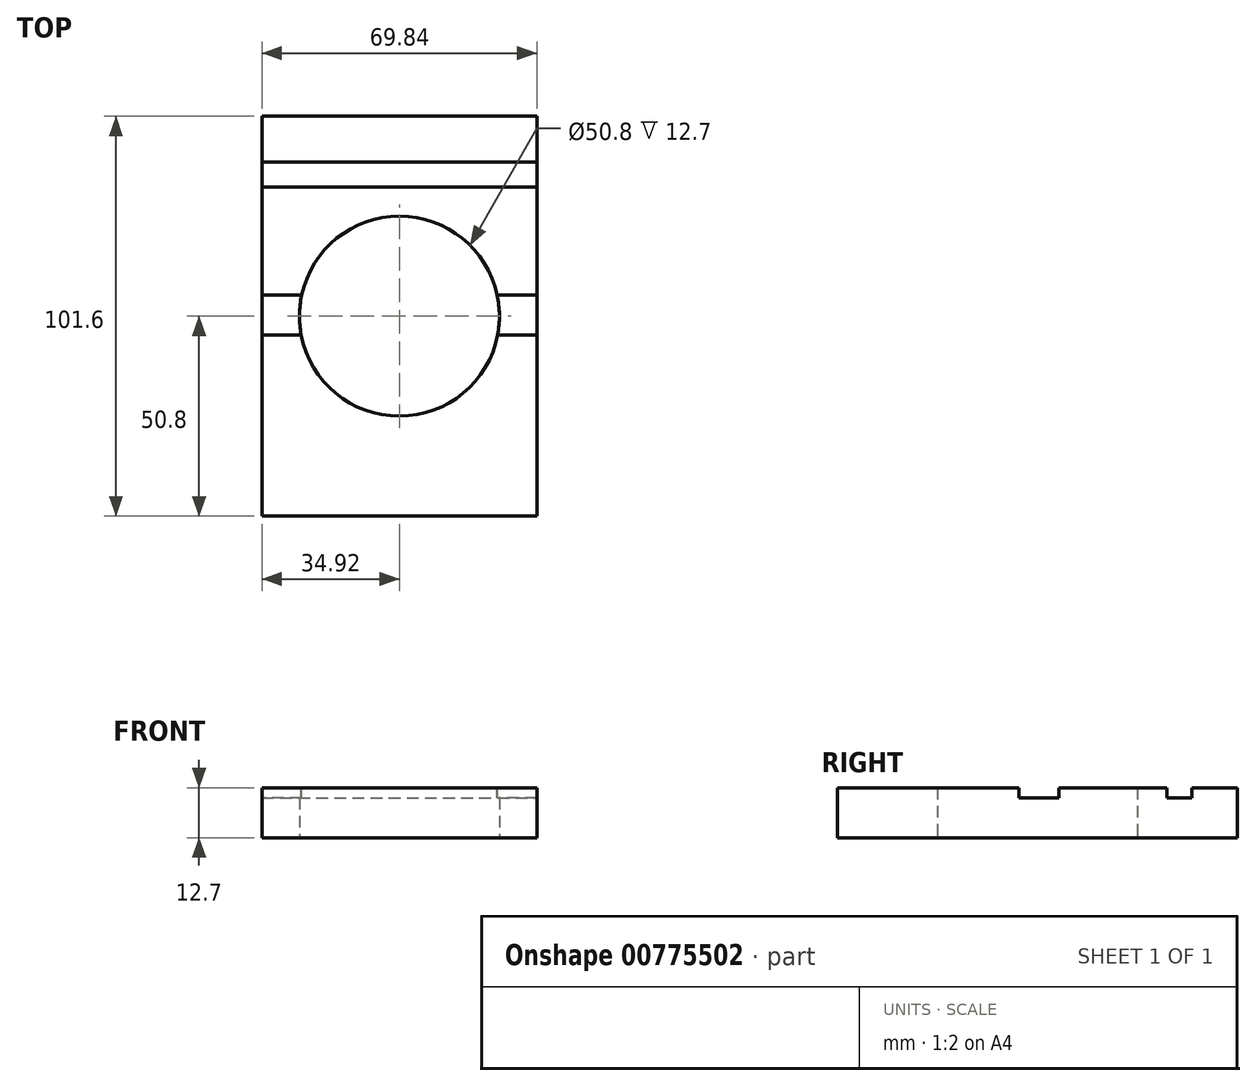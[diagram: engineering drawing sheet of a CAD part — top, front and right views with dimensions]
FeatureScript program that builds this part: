
annotation { "Feature Type Name" : "Feature", "Feature Type Description" : "" }
export const myFeature = defineFeature(function(context is Context, id is Id, definition is map)
    precondition{}
    {
        {
            var Q0;
            Q0=qCreatedBy(makeId("Top.planeOp"),FACE);
            var sketch = newSketch(context, id + "F0", { "sketchPlane" : qUnion([Q0])});
            skLineSegment(sketch, "E0.bottom", {"start": v(34.93, 50.8) * mm, "end": v(-34.92, 50.8) * mm});
            skLineSegment(sketch, "E0.top", {"start": v(34.92, -50.8) * mm, "end": v(-34.93, -50.8) * mm});
            skLineSegment(sketch, "E0.left", {"start": v(34.93, 50.8) * mm, "end": v(34.93, -50.8) * mm});
            skLineSegment(sketch, "E0.right", {"start": v(-34.92, 50.8) * mm, "end": v(-34.93, -50.8) * mm});
            skPoint(sketch, "E0.middle", {"position": v(0, 0) * mm});
            skCircle(sketch, "E1", {"center": v(0, 0) * mm, "radius": 25.4 * mm});
            skSolve(sketch);
        }
        {
            var Q0;
            Q0=makeQuery(id+"F0.imprint","IMPRINT",FACE,{"disambiguationData":[TD([[makeQuery(id+"F0.imprint","IMPRINT",EDGE,{"derivedFrom":sQuery(id+"F0.wireOp",EDGE,"E0.bottom")}),1.0]])]});
            extrude(context, id + "F1", {"entities" : qUnion([Q0]), "depth" : 12.7 * mm, "offsetDistance" : 25.4 * mm});
        }
        {
            var Q0;
            Q0=makeQuery(id+"F1.opExtrude","CAP_FACE",FACE,{"disambiguationData":[OSD([sQuery(id+"F0.wireOp",EDGE,"E0.bottom"),sQuery(id+"F0.wireOp",EDGE,"E0.top"),sQuery(id+"F0.wireOp",EDGE,"E0.left"),sQuery(id+"F0.wireOp",EDGE,"E0.right"),sQuery(id+"F0.wireOp",EDGE,"E1")])],"isStart":false});
            var sketch = newSketch(context, id + "F2", { "sketchPlane" : qUnion([Q0])});
            skLineSegment(sketch, "E2.bottom", {"start": v(-34.92, 39.2) * mm, "end": v(34.93, 39.2) * mm});
            skLineSegment(sketch, "E2.top", {"start": v(-34.92, 32.86) * mm, "end": v(34.93, 32.86) * mm});
            skLineSegment(sketch, "E2.left", {"start": v(-34.92, 39.2) * mm, "end": v(-34.92, 32.86) * mm});
            skLineSegment(sketch, "E2.right", {"start": v(34.93, 39.2) * mm, "end": v(34.93, 32.86) * mm});
            skLineSegment(sketch, "E3", {"start": v(34.93, 5.4) * mm, "end": v(-34.92, 5.4) * mm});
            skLineSegment(sketch, "E4", {"start": v(-34.92, 5.4) * mm, "end": v(-34.92, -4.76) * mm});
            skLineSegment(sketch, "E5", {"start": v(-34.92, -4.76) * mm, "end": v(34.93, -4.76) * mm});
            skLineSegment(sketch, "E6", {"start": v(34.93, -4.76) * mm, "end": v(34.93, 5.4) * mm});
            skPoint(sketch, "E7", {"position": v(0, 0) * mm});
            skPoint(sketch, "E8", {"position": v(34.93, 0.32) * mm});
            skPoint(sketch, "E9", {"position": v(34.97, -0.32) * mm});
            skPoint(sketch, "E10", {"position": v(-34.92, 0.32) * mm});
            skLineSegment(sketch, "E11", {"start": v(34.97, -0.32) * mm, "end": v(-34.92, 0.32) * mm});
            skSolve(sketch);
        }
        {
            var Q0;
            {var subQ0=sQuery(id+"F2.wireOp",EDGE,"E4");var subQ5=sQuery(id+"F2.wireOp",EDGE,"E11");var subQ6=makeQuery(id+"F2.imprint","INTERSECT",VERTEX,{"derivedFrom":[subQ0,subQ5]});Q0=makeQuery(id+"F2.imprint","IMPRINT",FACE,{"disambiguationData":[TD([[makeQuery(id+"F2.imprint","IMPRINT",EDGE,{"disambiguationData":[TD([[subQ6,1.0]])],"derivedFrom":subQ5}),-1.0]])]});}
            var Q1;
            {var subQ1=sQuery(id+"F2.wireOp",EDGE,"E4");var subQ3=sQuery(id+"F2.wireOp",EDGE,"E11");var subQ4=makeQuery(id+"F2.imprint","INTERSECT",VERTEX,{"derivedFrom":[subQ1,subQ3]});Q1=makeQuery(id+"F2.imprint","IMPRINT",FACE,{"disambiguationData":[TD([[makeQuery(id+"F2.imprint","IMPRINT",EDGE,{"disambiguationData":[TD([[subQ4,1.0]])],"derivedFrom":subQ3}),1.0]])]});}
            var Q2;
            {var subQ0=sQuery(id+"F2.wireOp",EDGE,"E6");var subQ5=sQuery(id+"F2.wireOp",EDGE,"E11");var subQ6=makeQuery(id+"F2.imprint","INTERSECT",VERTEX,{"derivedFrom":[subQ0,subQ5]});Q2=makeQuery(id+"F2.imprint","IMPRINT",FACE,{"disambiguationData":[TD([[makeQuery(id+"F2.imprint","IMPRINT",EDGE,{"disambiguationData":[TD([[subQ6,-1.0]])],"derivedFrom":subQ5}),-1.0]])]});}
            var Q3;
            {var subQ0=sQuery(id+"F2.wireOp",EDGE,"E6");var subQ5=sQuery(id+"F2.wireOp",EDGE,"E11");var subQ6=makeQuery(id+"F2.imprint","INTERSECT",VERTEX,{"derivedFrom":[subQ0,subQ5]});Q3=makeQuery(id+"F2.imprint","IMPRINT",FACE,{"disambiguationData":[TD([[makeQuery(id+"F2.imprint","IMPRINT",EDGE,{"disambiguationData":[TD([[subQ6,-1.0]])],"derivedFrom":subQ5}),1.0]])]});}
            var Q4;
            Q4=makeQuery(id+"F2.imprint","IMPRINT",FACE,{"disambiguationData":[TD([[makeQuery(id+"F2.imprint","IMPRINT",EDGE,{"derivedFrom":sQuery(id+"F2.wireOp",EDGE,"E2.bottom")}),-1.0]])]});
            extrude(context, id + "F3", {"entities" : qUnion([Q0, Q1, Q2, Q3, Q4]), "operationType" : NewBodyOperationType.REMOVE, "oppositeDirection" : true, "depth" : 2.54 * mm, "offsetDistance" : 25.4 * mm});
        }
    });
